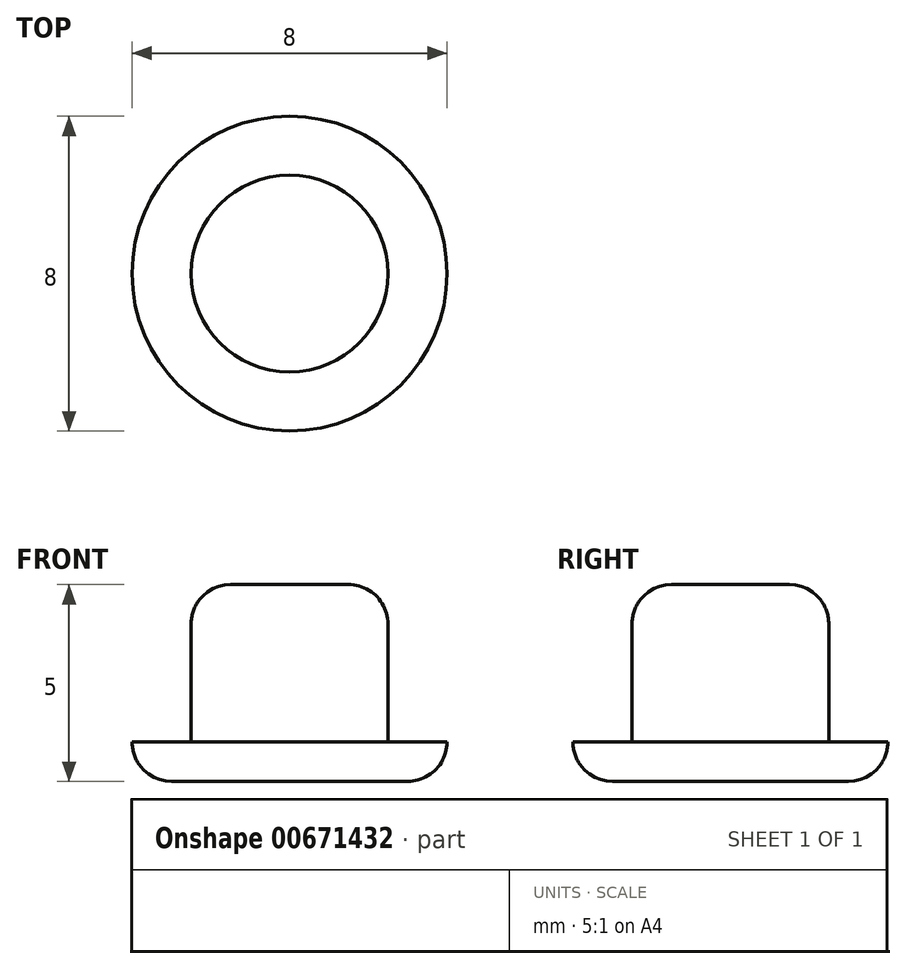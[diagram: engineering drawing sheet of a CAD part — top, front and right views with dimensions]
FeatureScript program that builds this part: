
annotation { "Feature Type Name" : "Feature", "Feature Type Description" : "" }
export const myFeature = defineFeature(function(context is Context, id is Id, definition is map)
    precondition{}
    {
        {
            var Q0;
            Q0=qCreatedBy(makeId("Top.planeOp"),FACE);
            var sketch = newSketch(context, id + "F0", { "sketchPlane" : qUnion([Q0])});
            skCircle(sketch, "E0", {"center": v(0, 0) * mm, "radius": 2.5 * mm});
            skCircle(sketch, "E1", {"center": v(0, 0) * mm, "radius": 4 * mm});
            skSolve(sketch);
        }
        {
            var Q0;
            Q0=makeQuery(id+"F0.imprint","IMPRINT",FACE,{"disambiguationData":[TD([[makeQuery(id+"F0.imprint","IMPRINT",EDGE,{"derivedFrom":sQuery(id+"F0.wireOp",EDGE,"E0")}),1.0]])]});
            extrude(context, id + "F1", {"entities" : qUnion([Q0]), "depth" : 5 * mm, "offsetDistance" : 25 * mm});
        }
        {
            var Q0;
            Q0=makeQuery(id+"F0.imprint","IMPRINT",FACE,{"disambiguationData":[TD([[makeQuery(id+"F0.imprint","IMPRINT",EDGE,{"derivedFrom":sQuery(id+"F0.wireOp",EDGE,"E0")}),-1.0]])]});
            extrude(context, id + "F2", {"entities" : qUnion([Q0]), "operationType" : NewBodyOperationType.ADD, "depth" : 1 * mm, "offsetDistance" : 25 * mm});
        }
        {
            var Q0;
            Q0=makeQuery(id+"F2.opExtrude","CAP_EDGE",EDGE,{"disambiguationData":[OSD([sQuery(id+"F0.wireOp",EDGE,"E1")])],"isStart":true});
            var Q1;
            Q1=makeQuery(id+"F1.opExtrude","CAP_EDGE",EDGE,{"disambiguationData":[OSD([sQuery(id+"F0.wireOp",EDGE,"E0")])],"isStart":false});
            fillet(context, id + "F3", {"entities" : qUnion([Q0, Q1]), "radius" : 1 * mm, "tangentPropagation" : true, "allowEdgeOverflow" : false});
        }
    });
